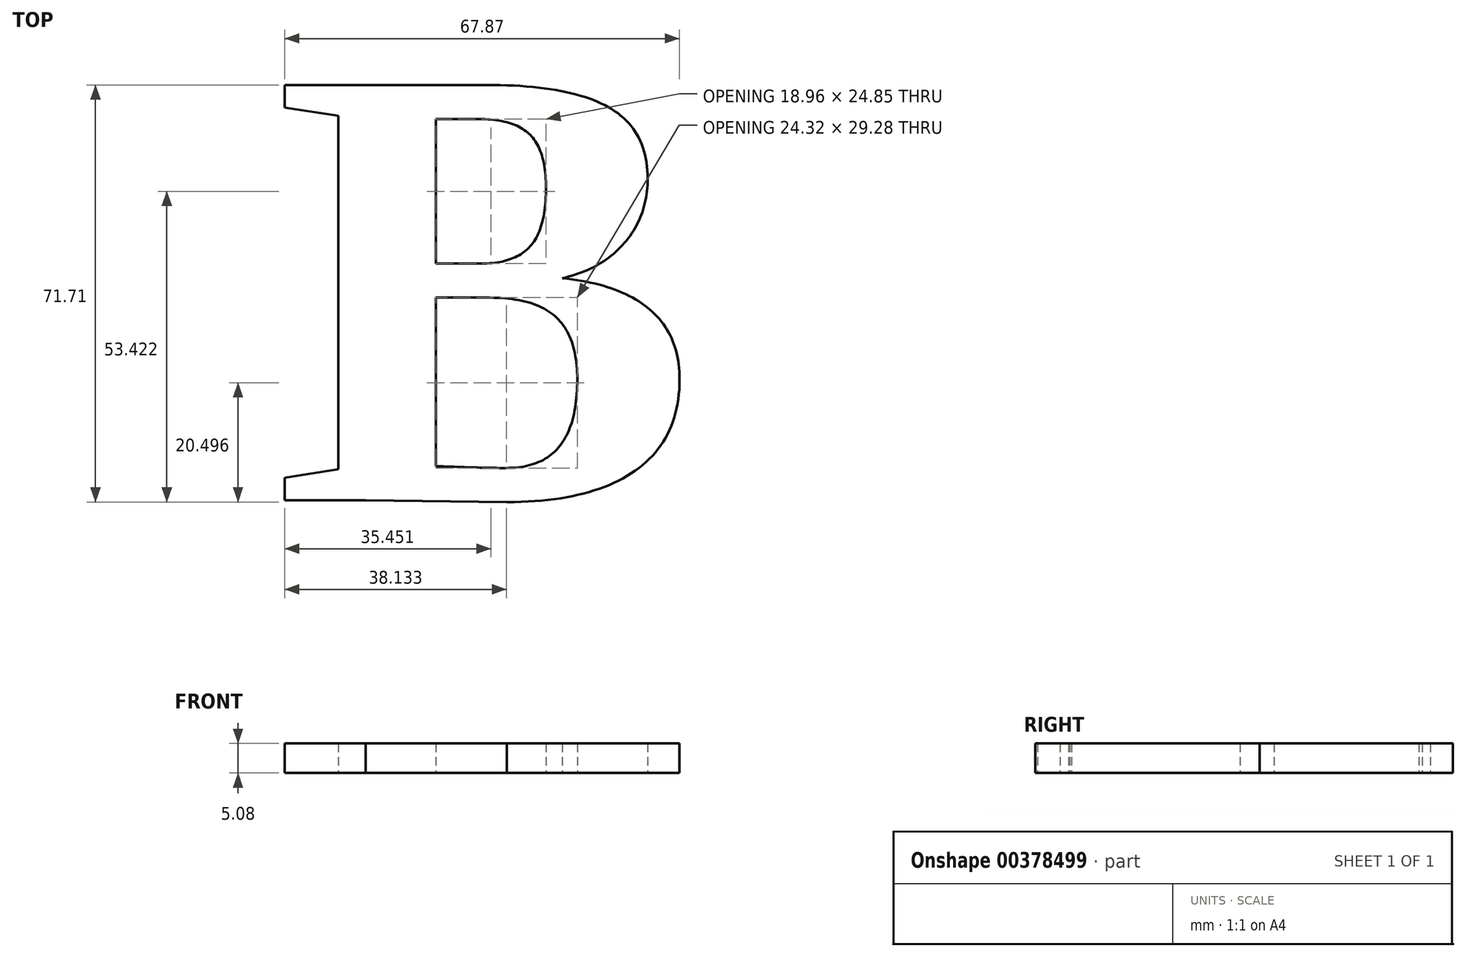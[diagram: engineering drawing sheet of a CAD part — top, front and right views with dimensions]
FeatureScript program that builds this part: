
annotation { "Feature Type Name" : "Feature", "Feature Type Description" : "" }
export const myFeature = defineFeature(function(context is Context, id is Id, definition is map)
    precondition{}
    {
        {
            var Q0;
            Q0=qCreatedBy(makeId("Top.planeOp"),FACE);
            var sketch = newSketch(context, id + "F0", { "sketchPlane" : qUnion([Q0])});
            skText(sketch, "E0", { "text": "B", "fontName": "Tinos-Bold.ttf"});
            const initialGuessF0  = {"E0": [-0.03555, -0.03874, 1, 0, 0.07849]};
            skSetInitialGuess(sketch, initialGuessF0);
            skSolve(sketch);
        }
        {
            var Q0;
            Q0 = qSketchRegion(id + "F0", true);
            extrude(context, id + "F1", {"entities" : qUnion([Q0]), "depth" : 5.08 * mm});
        }
    });
